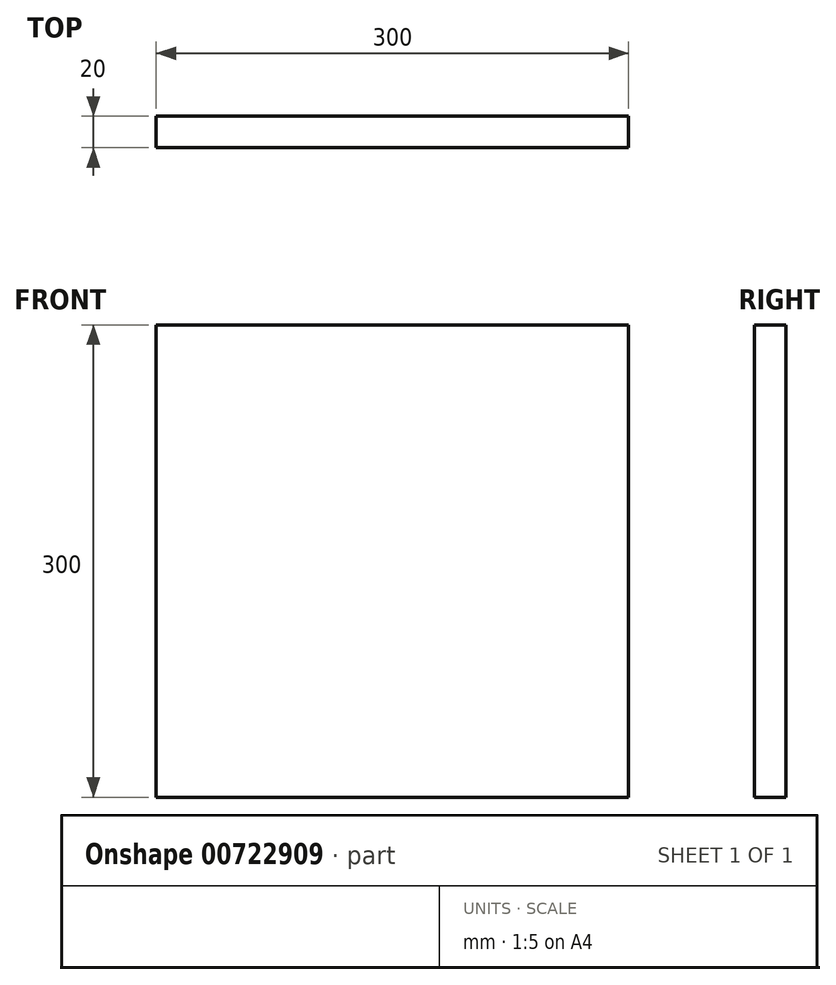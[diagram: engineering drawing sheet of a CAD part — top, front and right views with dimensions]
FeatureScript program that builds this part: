
annotation { "Feature Type Name" : "Feature", "Feature Type Description" : "" }
export const myFeature = defineFeature(function(context is Context, id is Id, definition is map)
    precondition{}
    {
        {
            var Q0;
            Q0=qCreatedBy(makeId("Front.planeOp"),FACE);
            var sketch = newSketch(context, id + "F0", { "sketchPlane" : qUnion([Q0])});
            skLineSegment(sketch, "E0.bottom", {"start": v(150, 150) * mm, "end": v(-150, 150) * mm});
            skLineSegment(sketch, "E0.top", {"start": v(150, -150) * mm, "end": v(-150, -150) * mm});
            skLineSegment(sketch, "E0.left", {"start": v(150, 150) * mm, "end": v(150, -150) * mm});
            skLineSegment(sketch, "E0.right", {"start": v(-150, 150) * mm, "end": v(-150, -150) * mm});
            skPoint(sketch, "E0.middle", {"position": v(0, 0) * mm});
            skSolve(sketch);
        }
        {
            var Q0;
            Q0=makeQuery(id+"F0.imprint","IMPRINT",FACE,{"disambiguationData":[TD([[makeQuery(id+"F0.imprint","IMPRINT",EDGE,{"derivedFrom":sQuery(id+"F0.wireOp",EDGE,"E0.bottom")}),1.0]])]});
            extrude(context, id + "F1", {"entities" : qUnion([Q0]), "depth" : 20 * mm, "offsetDistance" : 25 * mm});
        }
    });
